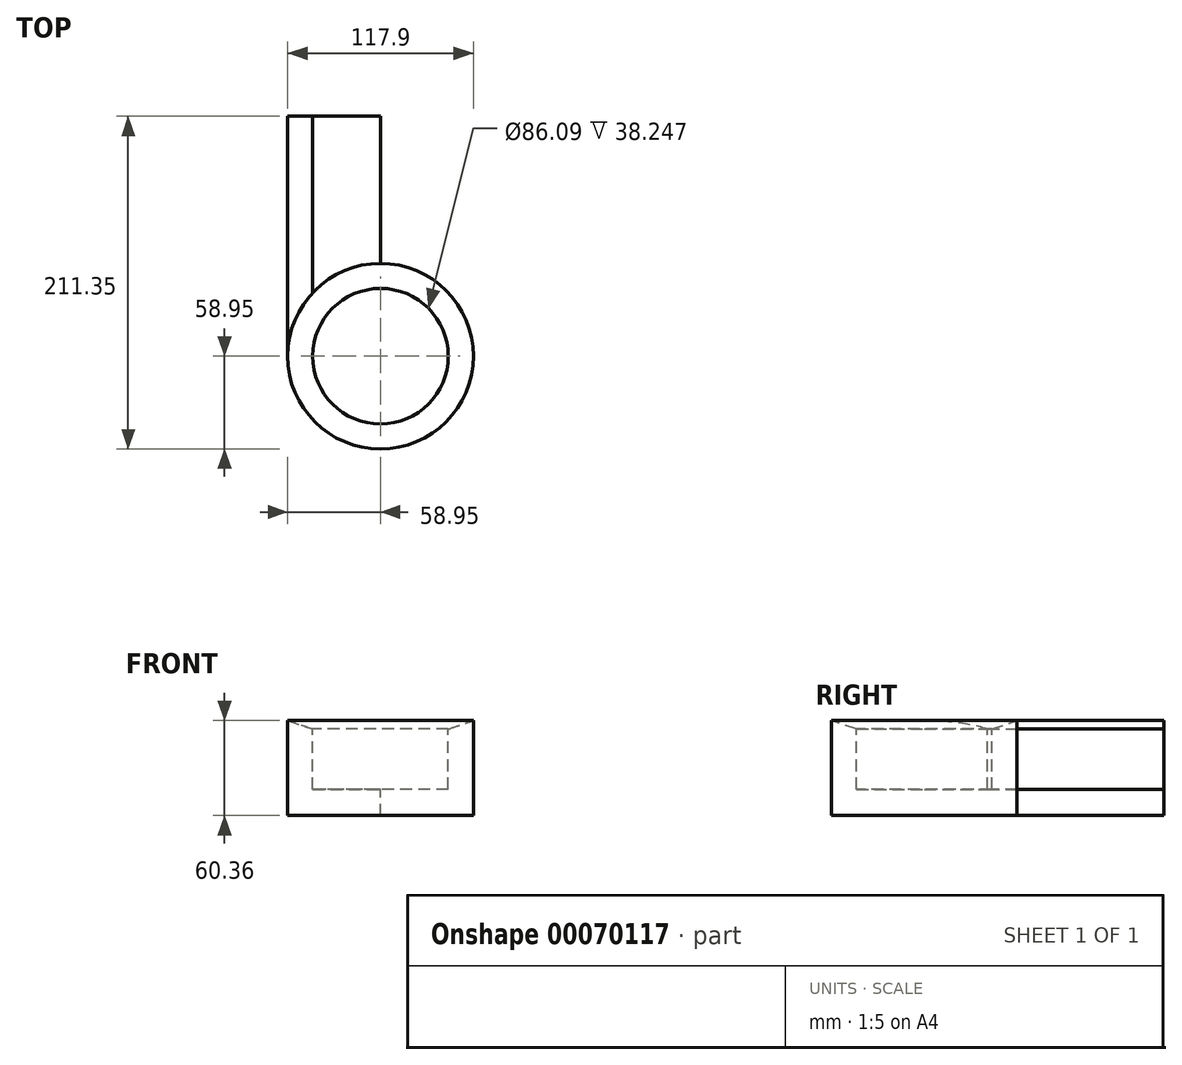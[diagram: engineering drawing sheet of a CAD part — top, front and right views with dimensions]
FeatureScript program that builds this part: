
annotation { "Feature Type Name" : "Feature", "Feature Type Description" : "" }
export const myFeature = defineFeature(function(context is Context, id is Id, definition is map)
    precondition{}
    {
        {
            var Q0;
            Q0=qCreatedBy(makeId("Front.planeOp"),FACE);
            var sketch = newSketch(context, id + "F0", { "sketchPlane" : qUnion([Q0])});
            skLineSegment(sketch, "E0", {"start": v(0, 0) * mm, "end": v(-58.95, 0) * mm});
            skLineSegment(sketch, "E1", {"start": v(-58.95, -0.16) * mm, "end": v(-58.95, 60.36) * mm});
            skLineSegment(sketch, "E2", {"start": v(-58.95, 60.36) * mm, "end": v(-43.05, 54.94) * mm});
            skLineSegment(sketch, "E3", {"start": v(-43.05, 54.94) * mm, "end": v(-43.05, 30.1) * mm});
            skPoint(sketch, "E4", {"position": v(-58.95, 30.1) * mm});
            skLineSegment(sketch, "E5", {"start": v(-43.05, 30.1) * mm, "end": v(-43.05, 16.69) * mm});
            skLineSegment(sketch, "E6", {"start": v(-43.05, 16.69) * mm, "end": v(0, 16.69) * mm});
            skLineSegment(sketch, "E7", {"start": v(0, 16.69) * mm, "end": v(0, 0) * mm});
            skSolve(sketch);
        }
        {
            var Q0;
            Q0 = qSketchRegion(id + "F0", true);
            extrude(context, id + "F1", {"entities" : qUnion([Q0]), "depth" : 152.4 * mm});
        }
        {
            var Q0;
            Q0=makeQuery(id+"F1.opExtrude","CAP_FACE",FACE,{"disambiguationData":[OSD([sQuery(id+"F0.wireOp",EDGE,"E0"),sQuery(id+"F0.wireOp",EDGE,"E1"),sQuery(id+"F0.wireOp",EDGE,"E2"),sQuery(id+"F0.wireOp",EDGE,"E3"),sQuery(id+"F0.wireOp",EDGE,"E5"),sQuery(id+"F0.wireOp",EDGE,"E6"),sQuery(id+"F0.wireOp",EDGE,"E7")])],"isStart":false});
            var Q1;
            Q1=makeQuery(id+"F1.opExtrude","CAP_EDGE",EDGE,{"disambiguationData":[OSD([sQuery(id+"F0.wireOp",EDGE,"E7")])],"isStart":false});
            revolve(context, id + "F2", {"operationType" : NewBodyOperationType.ADD, "entities" : qUnion([Q0]), "axis" : qUnion([Q1]), "revolveType" : RevolveType.FULL});
        }
    });
